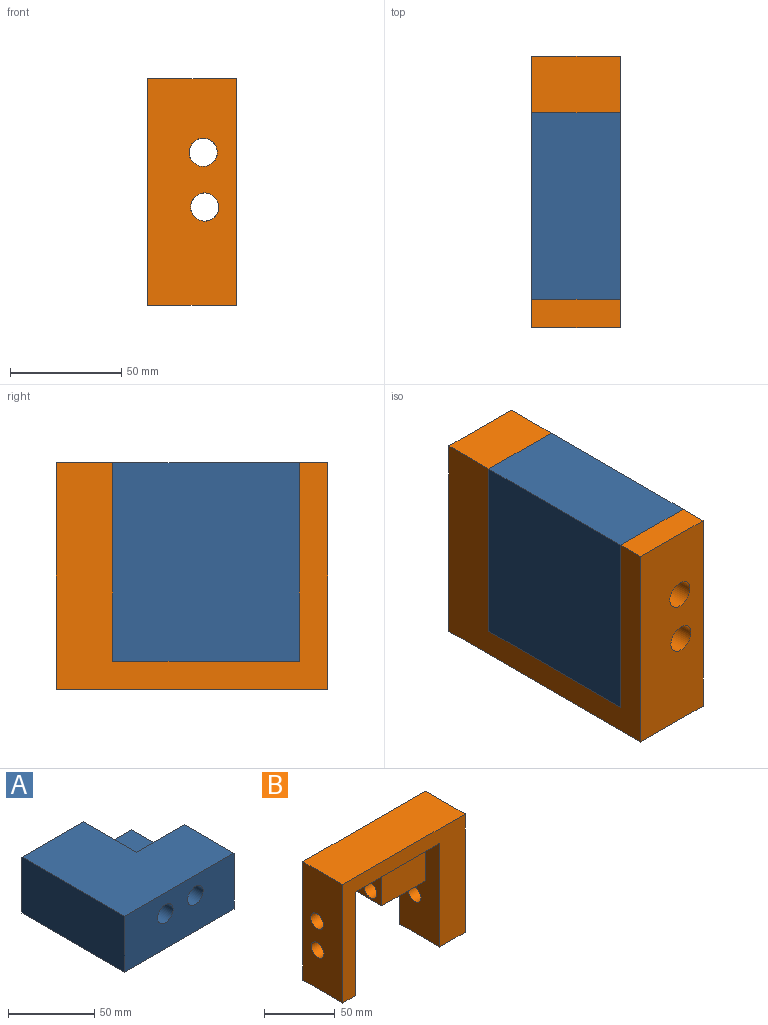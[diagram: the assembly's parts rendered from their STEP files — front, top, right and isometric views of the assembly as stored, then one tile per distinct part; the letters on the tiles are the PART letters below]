
ASSEMBLY  parts=2 mates=4
PART A: 11 faces, bbox 89.4x83.9x39.6 mm
  f0: plane 89.41x39.62mm, normal (0,1,0), area 2416.5mm2, adj f1,f2,f4,f6,f7,f9,f10
  f1: plane 83.94x39.62mm, normal (1,0,0), area 2224.7mm2, adj f0,f2,f5,f6,f8,f10
  f2: plane 89.41x83.94mm, normal (0,0,1), area 5798.7mm2, adj f0,f1,f4,f5,f8,f9
  f3: cylinder r=6.35mm len=40.58mm, axis (0,-1,0), area 1619.1mm2, adj f5,f8
  f4: plane 83.94x39.62mm, normal (-1,0,0), area 3326.1mm2, adj f0,f2,f5,f6
  f5: plane 89.41x39.62mm, normal (0,-1,0), area 3289.6mm2, adj f1,f2,f3,f4,f6,f7
  f6: plane 89.41x83.94mm, normal (0,0,-1), area 7505.5mm2, adj f0,f1,f4,f5
  f7: cylinder r=6.35mm len=83.94mm, axis (0,-1,0), area 3349.1mm2, adj f0,f5
  f8: plane 39.36x25.4mm, normal (0,1,0), area 873.1mm2, adj f1,f2,f3,f9,f10
  f9: plane 43.36x25.4mm, normal (1,0,0), area 1101.4mm2, adj f0,f2,f8,f10
  f10: plane 43.36x39.36mm, normal (0,0,1), area 1706.8mm2, adj f0,f1,f8,f9
PART B: 17 faces, bbox 122x39.6x102.1 mm
  f0: plane 83.94x39.62mm, normal (0,0,-1), area 2224.7mm2, adj f2,f4,f7,f8,f9,f12
  f1: plane 43.36x25.4mm, normal (0,0,-1), area 1101.4mm2, adj f2,f7,f8,f9
  f2: plane 122.04x102.11mm, normal (0,1,0), area 6663.4mm2, adj f0,f1,f3,f5,f6,f7,f9,f10
  f3: plane 102.11x39.62mm, normal (-1,0,0), area 3792.8mm2, adj f2,f4,f6,f11,f13,f14
  f4: plane 122.04x102.11mm, normal (0,-1,0), area 4956.6mm2, adj f0,f3,f5,f6,f9,f10,f11,f12
  f5: plane 102.11x39.62mm, normal (1,0,0), area 3792.8mm2, adj f2,f4,f6,f10,f15,f16
  f6: plane 122.04x39.62mm, normal (0,0,1), area 4835.8mm2, adj f2,f3,f4,f5
  f7: plane 39.36x25.4mm, normal (-1,0,0), area 873.1mm2, adj f0,f1,f2,f8,f16
  f8: plane 43.36x39.36mm, normal (0,-1,0), area 1706.8mm2, adj f0,f1,f7,f9
  f9: plane 89.41x39.62mm, normal (-1,0,0), area 2416.5mm2, adj f0,f1,f2,f4,f8,f10,f15
  f10: plane 39.62x25.4mm, normal (0,0,-1), area 1006.4mm2, adj f2,f4,f5,f9
  f11: plane 39.62x12.7mm, normal (0,0,-1), area 503.2mm2, adj f2,f3,f4,f12
  f12: plane 89.41x39.62mm, normal (1,0,0), area 3289.6mm2, adj f0,f2,f4,f11,f13,f14
  f13: cylinder r=6.35mm len=12.7mm, axis (-1,0,0), area 506.7mm2, adj f3,f12
  f14: cylinder r=6.35mm len=12.7mm, axis (-1,0,0), area 506.7mm2, adj f3,f12
  f15: cylinder r=6.35mm len=25.4mm, axis (-1,0,0), area 1013.4mm2, adj f5,f9
  f16: cylinder r=6.35mm len=68.76mm, axis (-1,0,0), area 2743.5mm2, adj f5,f7
PLACE A rot(axis=(0,1,0),90deg) t=(222.49,-49.83,212.38)mm fixed
PLACE B rot(axis=(0.71,0.71,0),180deg) t=(236.72,-93.2,122.97)mm
MATE planar A.f10 <-> B.f8  axis (1,0,0) through (236.72,-71.51,142.65)mm
MATE planar A.f4 <-> B.f11  axis (0,0,1) through (242.3,-91.8,212.38)mm
MATE planar B.f12 <-> A.f5  axis (0,1,0) through (241.89,-133.77,167.74)mm
MATE planar B.f5 <-> B.f6  axis (0,1,0) through (241.94,-24.43,160.96)mm
